# Revit family: Sanitary_Mirrors_Svedholm_Saturnus
name_source: partatom
category: Furniture
revit_build: Autodesk Revit 2018 (Build: 20190510_1515(x64)
units: mm (PartAtom-declared; Revit-internal decimal feet)

## family parameters
Cut with Voids When Loaded = No
Host = Face
OmniClass Number = 23.21.37.13.15
OmniClass Title = Mirrors
Room Calculation Point = No
Shared = No

## types (1)
- ART - (121.600.001)
    BIMobject category = Mirrors
    Default Elevation = 1219 mm
    Description = A mirror with chrome plated alternatively powder coated wire and powder coated steel frame.
    Design country = Sweden
    Edition number = 1
    IFC Classification = Object
    Manufacturer = Svedholm
    Manufacturer country = Sweden
    Manufacturer name = Svedholm
    Masterformat 2014 Code = 08 83 00
    Masterformat 2014 Description = Mirrors
    Material main = Mirror Glass
    Material secondary = Powder coated steel
    Mirror material = Svedholm - Glass - Mirror
    Model = Saturnus
    NBS Reference Code = 71-55
    NBS Reference Description = Mirrors
    OmniClass Code = 23-21 37 13 15
    OmniClass Description = Mirrors
    Product Guid = 61137649-7904-462c-8d7c-8853d0c54d98
    Product SKU = Saturnus
    Product data url = https://bimobject.com
    Product family = Saturnus
    Product group = Mirrors
    Product name = Saturnus
    Product url = https://www.svedholm.se
    QR code = https://bimobject.com
    URL = https://www.svedholm.se
    Uniclass 1.4 Code = L8732
    Uniclass 1.4 Description = Mirrors
    Uniclass 2.0 Code = PR-71-55
    Uniclass 2.0 Description = Mirrors
    Uniclass 2015 Code = Pr_25_71_53
    Uniclass 2015 Name = Mirrors

## geometry (parser evidence)
native form markers: Sweep x2
no freeform markers — native parametric forms only
